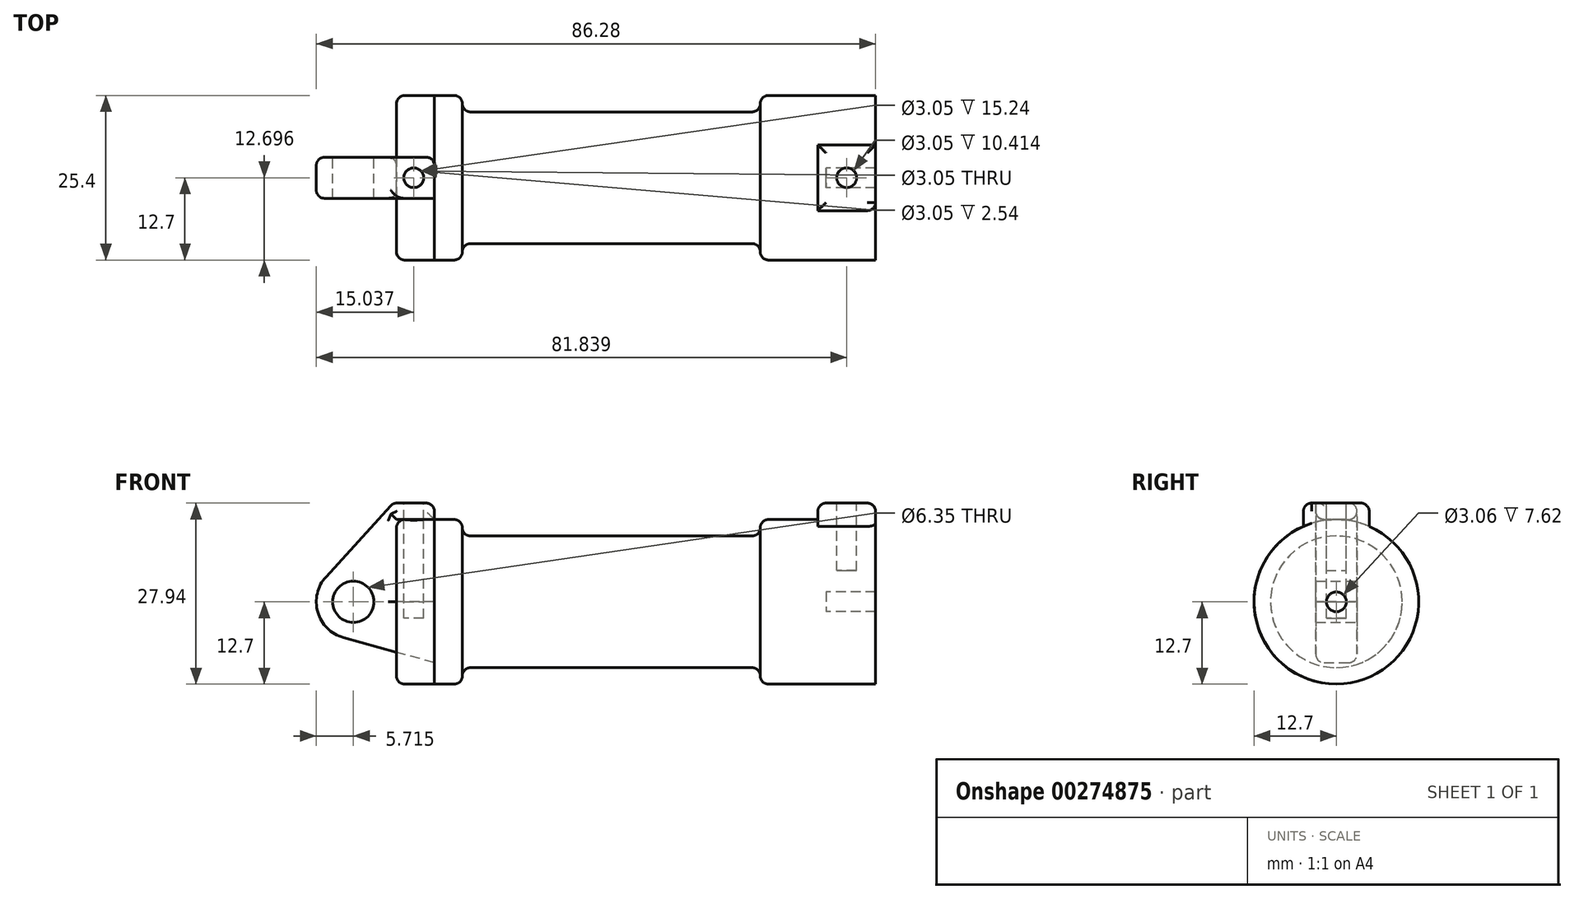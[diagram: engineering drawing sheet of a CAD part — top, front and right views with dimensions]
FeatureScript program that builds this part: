
annotation { "Feature Type Name" : "Feature", "Feature Type Description" : "" }
export const myFeature = defineFeature(function(context is Context, id is Id, definition is map)
    precondition{}
    {
        {
            var Q0;
            Q0=qCreatedBy(makeId("Front.planeOp"),FACE);
            var sketch = newSketch(context, id + "F0", { "sketchPlane" : qUnion([Q0])});
            skLineSegment(sketch, "E0", {"start": v(0, 0) * mm, "end": v(0, 12.7) * mm});
            skLineSegment(sketch, "E1", {"start": v(0, 12.7) * mm, "end": v(10.16, 12.7) * mm});
            skLineSegment(sketch, "E2", {"start": v(10.16, 12.7) * mm, "end": v(10.16, 10.16) * mm});
            skLineSegment(sketch, "E3", {"start": v(10.16, 10.16) * mm, "end": v(56.13, 10.16) * mm});
            skLineSegment(sketch, "E4", {"start": v(56.13, 10.16) * mm, "end": v(56.13, 12.7) * mm});
            skLineSegment(sketch, "E5", {"start": v(56.13, 12.7) * mm, "end": v(66.3, 12.7) * mm});
            skLineSegment(sketch, "E6", {"start": v(66.3, 12.7) * mm, "end": v(66.3, 0) * mm});
            skLineSegment(sketch, "E7", {"start": v(66.3, 0) * mm, "end": v(0, 0) * mm});
            skLineSegment(sketch, "E8", {"start": v(5.84, 15.24) * mm, "end": v(-0.5, 15.24) * mm});
            skLineSegment(sketch, "E9", {"start": v(-0.5, 15.24) * mm, "end": v(-10.88, 3.85) * mm});
            skLineSegment(sketch, "E10", {"start": v(0, 0) * mm, "end": v(-6.65, 0) * mm});
            skCircle(sketch, "E11", {"center": v(-6.65, 0) * mm, "radius": 5.72 * mm});
            skCircle(sketch, "E12", {"center": v(-6.65, 0) * mm, "radius": 3.18 * mm});
            skLineSegment(sketch, "E13", {"start": v(5.84, 15.24) * mm, "end": v(5.84, -9.4) * mm});
            skLineSegment(sketch, "E14", {"start": v(5.84, -9.4) * mm, "end": v(-8.18, -5.5) * mm});
            skSolve(sketch);
        }
        {
            var Q0;
            {var subQ0=sQuery(id+"F0.wireOp",EDGE,"E2");Q0=makeQuery(id+"F0.imprint","IMPRINT",FACE,{"disambiguationData":[TD([[makeQuery(id+"F0.imprint","IMPRINT",EDGE,{"derivedFrom":subQ0}),-1.0]])]});}
            var sketch = newSketch(context, id + "F1", { "sketchPlane" : qUnion([Q0])});
            skSolve(sketch);
        }
        {
            var Q0;
            {var subQ0=sQuery(id+"F0.wireOp",EDGE,"E2");Q0=makeQuery(id+"F1.imprint","IMPRINT",FACE,{"disambiguationData":[TD([[makeQuery(id+"F1.imprint","IMPRINT",EDGE,{"derivedFrom":makeQuery(id+"F0.imprint","IMPRINT",EDGE,{"derivedFrom":subQ0})}),-1.0]])]});}
            var Q1;
            {var subQ0=sQuery(id+"F0.wireOp",EDGE,"E0");Q1=makeQuery(id+"F0.imprint","IMPRINT",FACE,{"disambiguationData":[TD([[makeQuery(id+"F0.imprint","IMPRINT",EDGE,{"derivedFrom":subQ0}),-1.0]])]});}
            var Q2;
            Q2=sQuery(id+"F0.wireOp",EDGE,"E7");
            revolve(context, id + "F2", {"entities" : qUnion([Q0, Q1]), "axis" : qUnion([Q2]), "revolveType" : RevolveType.FULL});
        }
        {
            var Q0;
            {var subQ4=sQuery(id+"F0.wireOp",EDGE,"E12");Q0=makeQuery(id+"F0.imprint","IMPRINT",FACE,{"disambiguationData":[TD([[makeQuery(id+"F0.imprint","IMPRINT",EDGE,{"derivedFrom":subQ4}),-1.0]])]});}
            var Q1;
            {var subQ3=sQuery(id+"F0.wireOp",EDGE,"E0");Q1=makeQuery(id+"F0.imprint","IMPRINT",FACE,{"disambiguationData":[TD([[makeQuery(id+"F0.imprint","IMPRINT",EDGE,{"derivedFrom":subQ3}),1.0]])]});}
            var Q2;
            {var subQ0=sQuery(id+"F0.wireOp",EDGE,"E14");Q2=makeQuery(id+"F0.imprint","IMPRINT",FACE,{"disambiguationData":[TD([[makeQuery(id+"F0.imprint","IMPRINT",EDGE,{"derivedFrom":subQ0}),-1.0]])]});}
            extrude(context, id + "F3", {"entities" : qUnion([Q0, Q1, Q2]), "depth" : 3.17 * mm, "hasSecondDirection" : true, "secondDirectionOppositeDirection" : true, "secondDirectionDepth" : 3.17 * mm});
        }
        {
            var Q0;
            Q0=makeQuery(id+"F2.opRevolve","SWEPT_FACE",FACE,{"disambiguationData":[OSD([sQuery(id+"F0.wireOp",EDGE,"E6")])]});
            var sketch = newSketch(context, id + "F4", { "sketchPlane" : qUnion([Q0])});
            skCircle(sketch, "E15", {"center": v(0, 0) * mm, "radius": 1.53 * mm});
            skCircle(sketch, "E16", {"center": v(0, 0) * mm, "radius": 5.08 * mm});
            skLineSegment(sketch, "E17", {"start": v(0, 0) * mm, "end": v(5.08, 0) * mm});
            skLineSegment(sketch, "E18", {"start": v(5.08, 0) * mm, "end": v(-5.08, 0) * mm});
            skLineSegment(sketch, "E19", {"start": v(-5.08, 0) * mm, "end": v(-5.08, 15.24) * mm});
            skLineSegment(sketch, "E20", {"start": v(5.08, 0) * mm, "end": v(5.08, 15.24) * mm});
            skLineSegment(sketch, "E21", {"start": v(5.08, 15.24) * mm, "end": v(-5.08, 15.24) * mm});
            skSolve(sketch);
        }
        {
            var Q0;
            {var subQ0=sQuery(id+"F4.wireOp",EDGE,"E18");var subQ1=sQuery(id+"F4.wireOp",EDGE,"E15");var subQ2=makeQuery(id+"F4.imprint","INTERSECT",VERTEX,{"disambiguationData":[OD(0.0)],"derivedFrom":[subQ1,subQ0]});Q0=makeQuery(id+"F4.imprint","IMPRINT",FACE,{"disambiguationData":[TD([[makeQuery(id+"F4.imprint","IMPRINT",EDGE,{"disambiguationData":[TD([[subQ2,-1.0]])],"derivedFrom":subQ1}),-1.0]])]});}
            var Q1;
            {var subQ0=sQuery(id+"F4.wireOp",EDGE,"E18");var subQ1=sQuery(id+"F4.wireOp",EDGE,"E15");var subQ2=makeQuery(id+"F4.imprint","INTERSECT",VERTEX,{"disambiguationData":[OD(0.0)],"derivedFrom":[subQ1,subQ0]});Q1=makeQuery(id+"F4.imprint","IMPRINT",FACE,{"disambiguationData":[TD([[makeQuery(id+"F4.imprint","IMPRINT",EDGE,{"disambiguationData":[TD([[subQ2,1.0]])],"derivedFrom":subQ1}),-1.0]])]});}
            var Q2;
            {var subQ0=sQuery(id+"F4.wireOp",EDGE,"E20");var subQ1=sQuery(id+"F4.wireOp",EDGE,"E18");var subQ2=sQuery(id+"F4.wireOp",EDGE,"E16");var subQ3=makeQuery(id+"F4.imprint","INTERSECT",VERTEX,{"derivedFrom":[subQ2,subQ1,subQ0]});Q2=makeQuery(id+"F4.imprint","IMPRINT",FACE,{"disambiguationData":[TD([[makeQuery(id+"F4.imprint","IMPRINT",EDGE,{"disambiguationData":[TD([[subQ3,-1.0]])],"derivedFrom":subQ2}),-1.0]])]});}
            var Q3;
            {var subQ0=sQuery(id+"F4.wireOp",EDGE,"E21");Q3=makeQuery(id+"F4.imprint","IMPRINT",FACE,{"disambiguationData":[TD([[makeQuery(id+"F4.imprint","IMPRINT",EDGE,{"derivedFrom":subQ0}),1.0]])]});}
            extrude(context, id + "F5", {"entities" : qUnion([Q0, Q1, Q2, Q3]), "operationType" : NewBodyOperationType.ADD, "depth" : 7.62 * mm, "hasSecondDirection" : true, "secondDirectionOppositeDirection" : true, "secondDirectionDepth" : 1.27 * mm});
        }
        {
            var Q0;
            Q0=makeQuery(id+"F5.opExtrude","SWEPT_FACE",FACE,{"disambiguationData":[OSD([sQuery(id+"F4.wireOp",EDGE,"E21")])]});
            var sketch = newSketch(context, id + "F6", { "sketchPlane" : qUnion([Q0])});
            skCircle(sketch, "E22", {"center": v(69.47, -0.01) * mm, "radius": 1.53 * mm});
            skSolve(sketch);
        }
        {
            var Q0;
            Q0=makeQuery(id+"F6.imprint","IMPRINT",FACE,{"disambiguationData":[TD([[makeQuery(id+"F6.imprint","IMPRINT",EDGE,{"derivedFrom":sQuery(id+"F6.wireOp",EDGE,"E22")}),1.0]])]});
            var Q1;
            Q1=sQuery(id+"F6.wireOp",EDGE,"E22");
            extrude(context, id + "F7", {"entities" : qUnion([Q0]), "operationType" : NewBodyOperationType.REMOVE, "surfaceEntities" : qUnion([Q1]), "oppositeDirection" : true, "depth" : 10.4 * mm});
        }
        {
            var Q0;
            Q0=makeQuery(id+"F3.opExtrude","SWEPT_FACE",FACE,{"disambiguationData":[OSD([sQuery(id+"F0.wireOp",EDGE,"E8")])]});
            var sketch = newSketch(context, id + "F8", { "sketchPlane" : qUnion([Q0])});
            skCircle(sketch, "E23", {"center": v(2.67, 0) * mm, "radius": 1.52 * mm});
            skSolve(sketch);
        }
        {
            var Q0;
            Q0=makeQuery(id+"F8.imprint","IMPRINT",FACE,{"disambiguationData":[TD([[makeQuery(id+"F8.imprint","IMPRINT",EDGE,{"derivedFrom":sQuery(id+"F8.wireOp",EDGE,"E23")}),1.0]])]});
            extrude(context, id + "F9", {"entities" : qUnion([Q0]), "operationType" : NewBodyOperationType.REMOVE, "oppositeDirection" : true, "depth" : 17.78 * mm});
        }
        {
            var Q0;
            Q0=makeQuery(id+"F2.opRevolve","SWEPT_EDGE",EDGE,{"disambiguationData":[OSD([sQuery(id+"F0.wireOp",EDGE,"E1"),sQuery(id+"F0.wireOp",EDGE,"E2")])]});
            var Q1;
            Q1=makeQuery(id+"F2.opRevolve","SWEPT_FACE",FACE,{"disambiguationData":[OSD([sQuery(id+"F0.wireOp",EDGE,"E3")])]});
            var Q2;
            Q2=makeQuery(id+"F2.opRevolve","SWEPT_EDGE",EDGE,{"disambiguationData":[OSD([sQuery(id+"F0.wireOp",EDGE,"E0"),sQuery(id+"F0.wireOp",EDGE,"E1")])]});
            var Q3;
            Q3=makeQuery(id+"F2.opRevolve","SWEPT_EDGE",EDGE,{"disambiguationData":[OSD([sQuery(id+"F0.wireOp",EDGE,"E4"),sQuery(id+"F0.wireOp",EDGE,"E5")])]});
            var Q4;
            Q4=makeQuery(id+"F2.opRevolve","SWEPT_EDGE",EDGE,{"disambiguationData":[OSD([sQuery(id+"F0.wireOp",EDGE,"E5"),sQuery(id+"F0.wireOp",EDGE,"E6")])]});
            var Q5;
            {var subQ0=sQuery(id+"F0.wireOp",EDGE,"E13");Q5=makeQuery(id+"F3.opExtrude","CAP_EDGE",EDGE,{"disambiguationData":[OSD([subQ0]),TDD([makeQuery(id+"F0.imprint","IMPRINT",EDGE,{"disambiguationData":[TD([[makeQuery(id+"F0.imprint","INTERSECT",VERTEX,{"derivedFrom":[sQuery(id+"F0.wireOp",EDGE,"E8"),subQ0]}),-1.0]])],"derivedFrom":subQ0})])],"isStart":true});}
            var Q6;
            Q6=makeQuery(id+"F3.opExtrude","CAP_EDGE",EDGE,{"disambiguationData":[OSD([sQuery(id+"F0.wireOp",EDGE,"E8")])],"isStart":true});
            var Q7;
            Q7=makeQuery(id+"F3.opExtrude","CAP_EDGE",EDGE,{"disambiguationData":[OSD([sQuery(id+"F0.wireOp",EDGE,"E9")])],"isStart":true});
            var Q8;
            Q8=makeQuery(id+"F3.opExtrude","CAP_EDGE",EDGE,{"disambiguationData":[OSD([sQuery(id+"F0.wireOp",EDGE,"E0")])],"isStart":true});
            var Q9;
            Q9=makeQuery(id+"F3.opExtrude","CAP_EDGE",EDGE,{"disambiguationData":[OSD([sQuery(id+"F0.wireOp",EDGE,"E1")])],"isStart":true});
            var Q10;
            Q10=makeQuery(id+"F3.opExtrude","CAP_EDGE",EDGE,{"disambiguationData":[OSD([sQuery(id+"F0.wireOp",EDGE,"E0")])],"isStart":false});
            var Q11;
            Q11=makeQuery(id+"F3.opExtrude","SWEPT_EDGE",EDGE,{"disambiguationData":[OSD([sQuery(id+"F0.wireOp",EDGE,"E8"),sQuery(id+"F0.wireOp",EDGE,"E13")])]});
            var Q12;
            Q12=makeQuery(id+"F3.opExtrude","CAP_EDGE",EDGE,{"disambiguationData":[OSD([sQuery(id+"F0.wireOp",EDGE,"E9")])],"isStart":false});
            var Q13;
            Q13=makeQuery(id+"F3.opExtrude","SWEPT_EDGE",EDGE,{"disambiguationData":[OSD([sQuery(id+"F0.wireOp",EDGE,"E8"),sQuery(id+"F0.wireOp",EDGE,"E9")])]});
            var Q14;
            Q14=makeQuery(id+"F3.opExtrude","CAP_EDGE",EDGE,{"disambiguationData":[OSD([sQuery(id+"F0.wireOp",EDGE,"E1")])],"isStart":false});
            var Q15;
            Q15=makeQuery(id+"F5.opExtrude","SWEPT_EDGE",EDGE,{"disambiguationData":[OSD([sQuery(id+"F4.wireOp",EDGE,"E19"),sQuery(id+"F4.wireOp",EDGE,"E21")])]});
            var Q16;
            Q16=makeQuery(id+"F5.opExtrude","CAP_EDGE",EDGE,{"disambiguationData":[OSD([sQuery(id+"F4.wireOp",EDGE,"E19")])],"isStart":false});
            var Q17;
            Q17=makeQuery(id+"F5.opExtrude","SWEPT_FACE",FACE,{"disambiguationData":[OSD([sQuery(id+"F4.wireOp",EDGE,"E16")])]});
            var Q18;
            Q18=makeQuery(id+"F5.opExtrude","SWEPT_EDGE",EDGE,{"disambiguationData":[OSD([sQuery(id+"F4.wireOp",EDGE,"E20"),sQuery(id+"F4.wireOp",EDGE,"E21")])]});
            var Q19;
            Q19=makeQuery(id+"F5.opExtrude","CAP_EDGE",EDGE,{"disambiguationData":[OSD([sQuery(id+"F4.wireOp",EDGE,"E21")])],"isStart":false});
            var Q20;
            Q20=makeQuery(id+"F5.opExtrude","CAP_EDGE",EDGE,{"disambiguationData":[OSD([sQuery(id+"F4.wireOp",EDGE,"E21")])],"isStart":true});
            fillet(context, id + "F10", {"entities" : qUnion([Q0, Q1, Q2, Q3, Q4, Q5, Q6, Q7, Q8, Q9, Q10, Q11, Q12, Q13, Q14, Q15, Q16, Q17, Q18, Q19, Q20]), "radius" : 1.27 * mm, "tangentPropagation" : true, "allowEdgeOverflow" : false});
        }
    });
